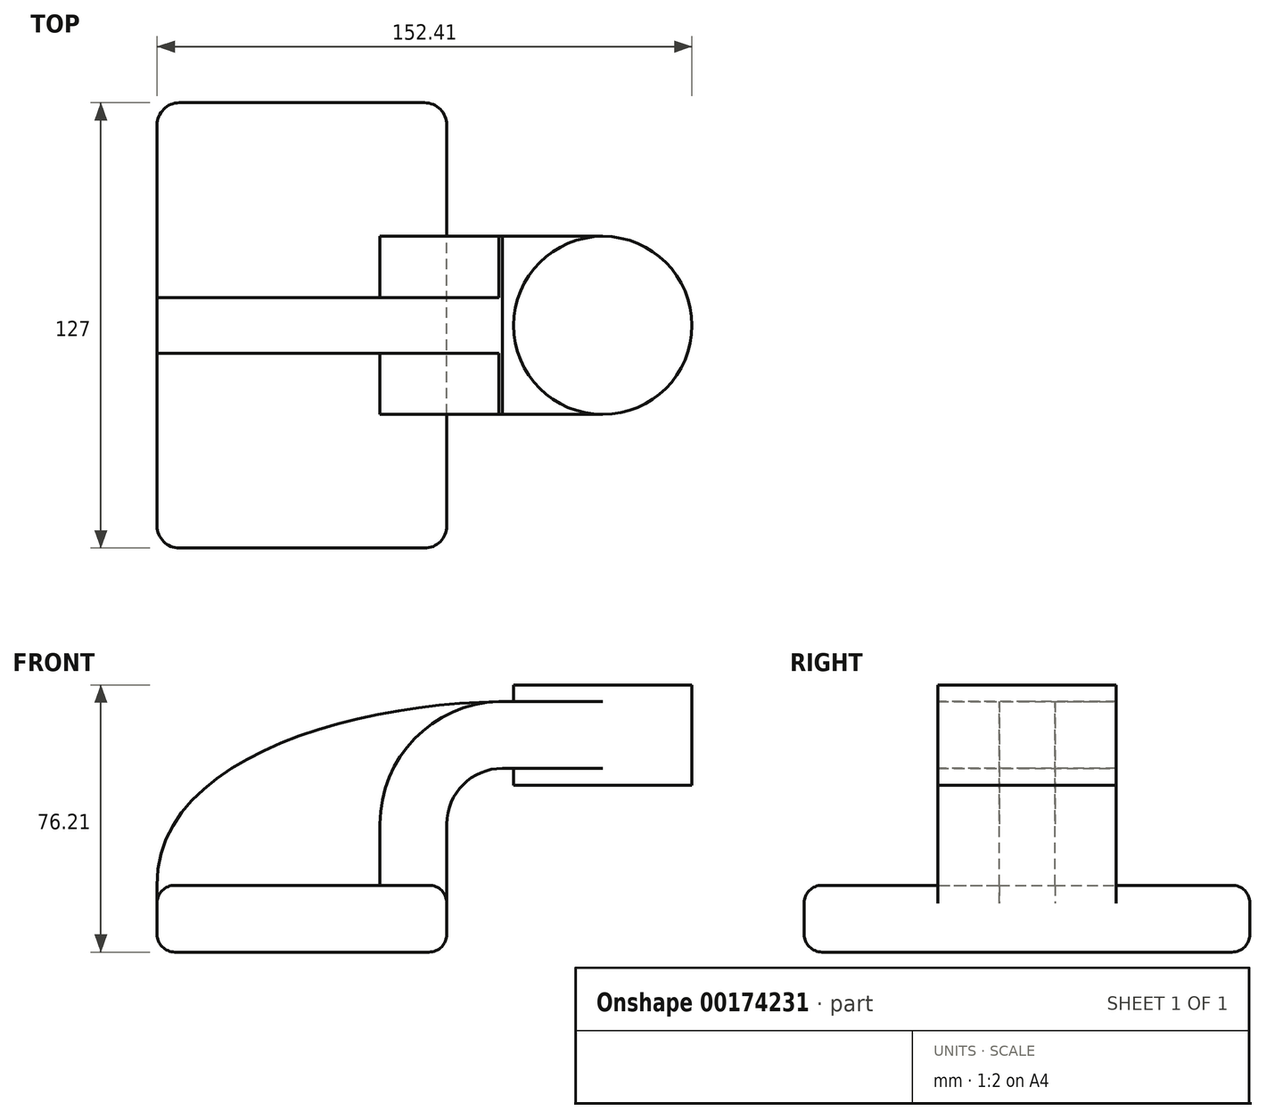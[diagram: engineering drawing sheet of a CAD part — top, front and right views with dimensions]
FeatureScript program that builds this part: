
annotation { "Feature Type Name" : "Feature", "Feature Type Description" : "" }
export const myFeature = defineFeature(function(context is Context, id is Id, definition is map)
    precondition{}
    {
        {
            var Q0;
            Q0=qCreatedBy(makeId("Front.planeOp"),FACE);
            var sketch = newSketch(context, id + "F0", { "sketchPlane" : qUnion([Q0])});
            skLineSegment(sketch, "E0.bottom", {"start": v(-41.28, 9.52) * mm, "end": v(41.28, 9.53) * mm});
            skLineSegment(sketch, "E0.top", {"start": v(-41.28, -9.53) * mm, "end": v(41.28, -9.53) * mm});
            skLineSegment(sketch, "E0.left", {"start": v(-41.28, 9.52) * mm, "end": v(-41.28, -9.53) * mm});
            skLineSegment(sketch, "E0.right", {"start": v(41.28, 9.53) * mm, "end": v(41.28, -9.52) * mm});
            skPoint(sketch, "E0.middle", {"position": v(0, 0) * mm});
            skLineSegment(sketch, "E1.bottom", {"start": v(60.32, 66.67) * mm, "end": v(111.12, 66.67) * mm});
            skLineSegment(sketch, "E1.top", {"start": v(60.33, 38.1) * mm, "end": v(111.12, 38.1) * mm});
            skLineSegment(sketch, "E1.left", {"start": v(60.32, 66.67) * mm, "end": v(60.33, 38.1) * mm});
            skLineSegment(sketch, "E1.right", {"start": v(111.12, 66.67) * mm, "end": v(111.12, 38.1) * mm});
            skPoint(sketch, "E1.middle", {"position": v(85.72, 52.39) * mm});
            skLineSegment(sketch, "E2", {"start": v(41.27, 9.53) * mm, "end": v(41.27, 27) * mm});
            skArc(sketch, "E3", {"start": v(41.27, 27) * mm, "mid": v(45.92, 38.23) * mm, "end": v(57.15, 42.88) * mm});
            skLineSegment(sketch, "E4", {"start": v(57.15, 42.88) * mm, "end": v(85.72, 42.88) * mm});
            skLineSegment(sketch, "E5.0", {"start": v(57.15, 61.93) * mm, "end": v(85.72, 61.93) * mm});
            skArc(sketch, "E5.1", {"start": v(22.22, 27) * mm, "mid": v(32.45, 51.7) * mm, "end": v(57.15, 61.93) * mm});
            skLineSegment(sketch, "E5.2", {"start": v(22.22, 9.53) * mm, "end": v(22.22, 27) * mm});
            skLineSegment(sketch, "E6", {"start": v(85.72, 38.1) * mm, "end": v(85.72, 66.67) * mm});
            skFitSpline(sketch, "E7", {"points": [v(-41.28, 9.52) * mm, v(57.15, 61.93) * mm], "startDerivative": vector(-1.14, 109.42) * mm, "endDerivative": vector(126.4, 1.55) * mm});
            skSolve(sketch);
        }
        {
            var Q0;
            Q0=makeQuery(id+"F0.imprint","IMPRINT",FACE,{"disambiguationData":[TD([[makeQuery(id+"F0.imprint","IMPRINT",EDGE,{"derivedFrom":sQuery(id+"F0.wireOp",EDGE,"E0.top")}),1.0]])]});
            extrude(context, id + "F1", {"entities" : qUnion([Q0]), "endBound" : BoundingType.SYMMETRIC, "depth" : 127 * mm});
        }
        {
            var Q0;
            {var subQ1=sQuery(id+"F0.wireOp",EDGE,"E2");Q0=makeQuery(id+"F0.imprint","IMPRINT",FACE,{"disambiguationData":[TD([[makeQuery(id+"F0.imprint","IMPRINT",EDGE,{"derivedFrom":subQ1}),1.0]])]});}
            var Q1;
            {var subQ0=sQuery(id+"F0.wireOp",EDGE,"E5.0");var subQ1=sQuery(id+"F0.wireOp",EDGE,"E1.left");var subQ2=makeQuery(id+"F0.imprint","INTERSECT",VERTEX,{"derivedFrom":[subQ1,subQ0]});Q1=makeQuery(id+"F0.imprint","IMPRINT",FACE,{"disambiguationData":[TD([[makeQuery(id+"F0.imprint","IMPRINT",EDGE,{"disambiguationData":[TD([[subQ2,-1.0]])],"derivedFrom":subQ1}),1.0]])]});}
            extrude(context, id + "F2", {"entities" : qUnion([Q0, Q1]), "operationType" : NewBodyOperationType.ADD, "endBound" : BoundingType.SYMMETRIC, "depth" : 50.8 * mm});
        }
        {
            var Q0;
            {var subQ3=sQuery(id+"F0.wireOp",EDGE,"E5.2");Q0=makeQuery(id+"F0.imprint","IMPRINT",FACE,{"disambiguationData":[TD([[makeQuery(id+"F0.imprint","IMPRINT",EDGE,{"derivedFrom":subQ3}),1.0]])]});}
            extrude(context, id + "F3", {"entities" : qUnion([Q0]), "operationType" : NewBodyOperationType.ADD, "endBound" : BoundingType.SYMMETRIC, "depth" : 15.88 * mm});
        }
        {
            var Q0;
            {var subQ0=sQuery(id+"F0.wireOp",EDGE,"E1.right");Q0=makeQuery(id+"F0.imprint","IMPRINT",FACE,{"disambiguationData":[TD([[makeQuery(id+"F0.imprint","IMPRINT",EDGE,{"derivedFrom":subQ0}),-1.0]])]});}
            var Q1;
            Q1=sQuery(id+"F0.wireOp",EDGE,"E6");
            revolve(context, id + "F4", {"operationType" : NewBodyOperationType.ADD, "entities" : qUnion([Q0]), "axis" : qUnion([Q1]), "revolveType" : RevolveType.FULL});
        }
        {
            var Q0;
            Q0=makeQuery(id+"F1.opExtrude","CAP_EDGE",EDGE,{"disambiguationData":[OSD([sQuery(id+"F0.wireOp",EDGE,"E0.left")])],"isStart":false});
            var Q1;
            Q1=makeQuery(id+"F1.opExtrude","CAP_EDGE",EDGE,{"disambiguationData":[OSD([sQuery(id+"F0.wireOp",EDGE,"E0.right")])],"isStart":false});
            var Q2;
            Q2=makeQuery(id+"F1.opExtrude","CAP_EDGE",EDGE,{"disambiguationData":[OSD([sQuery(id+"F0.wireOp",EDGE,"E0.right")])],"isStart":true});
            var Q3;
            Q3=makeQuery(id+"F1.opExtrude","CAP_EDGE",EDGE,{"disambiguationData":[OSD([sQuery(id+"F0.wireOp",EDGE,"E0.left")])],"isStart":true});
            fillet(context, id + "F5", {"entities" : qUnion([Q0, Q1, Q2, Q3]), "radius" : 6.35 * mm, "tangentPropagation" : true, "allowEdgeOverflow" : false});
        }
        {
            var Q0;
            Q0=makeQuery(id+"F1.opExtrude","CAP_EDGE",EDGE,{"disambiguationData":[OSD([sQuery(id+"F0.wireOp",EDGE,"E0.top")])],"isStart":false});
            fillet(context, id + "F6", {"entities" : qUnion([Q0]), "radius" : 5.08 * mm, "tangentPropagation" : true, "allowEdgeOverflow" : false});
        }
        {
            var Q0;
            Q0=makeQuery(id+"F1.opExtrude","CAP_EDGE",EDGE,{"disambiguationData":[OSD([sQuery(id+"F0.wireOp",EDGE,"E0.bottom")])],"isStart":true});
            fillet(context, id + "F7", {"entities" : qUnion([Q0]), "radius" : 5.08 * mm, "tangentPropagation" : true, "allowEdgeOverflow" : false});
        }
        {
            var Q0;
            Q0=makeQuery(id+"F1.opExtrude","CAP_EDGE",EDGE,{"disambiguationData":[OSD([sQuery(id+"F0.wireOp",EDGE,"E0.bottom")])],"isStart":false});
            fillet(context, id + "F8", {"entities" : qUnion([Q0]), "radius" : 5.08 * mm, "tangentPropagation" : true, "allowEdgeOverflow" : false});
        }
    });
